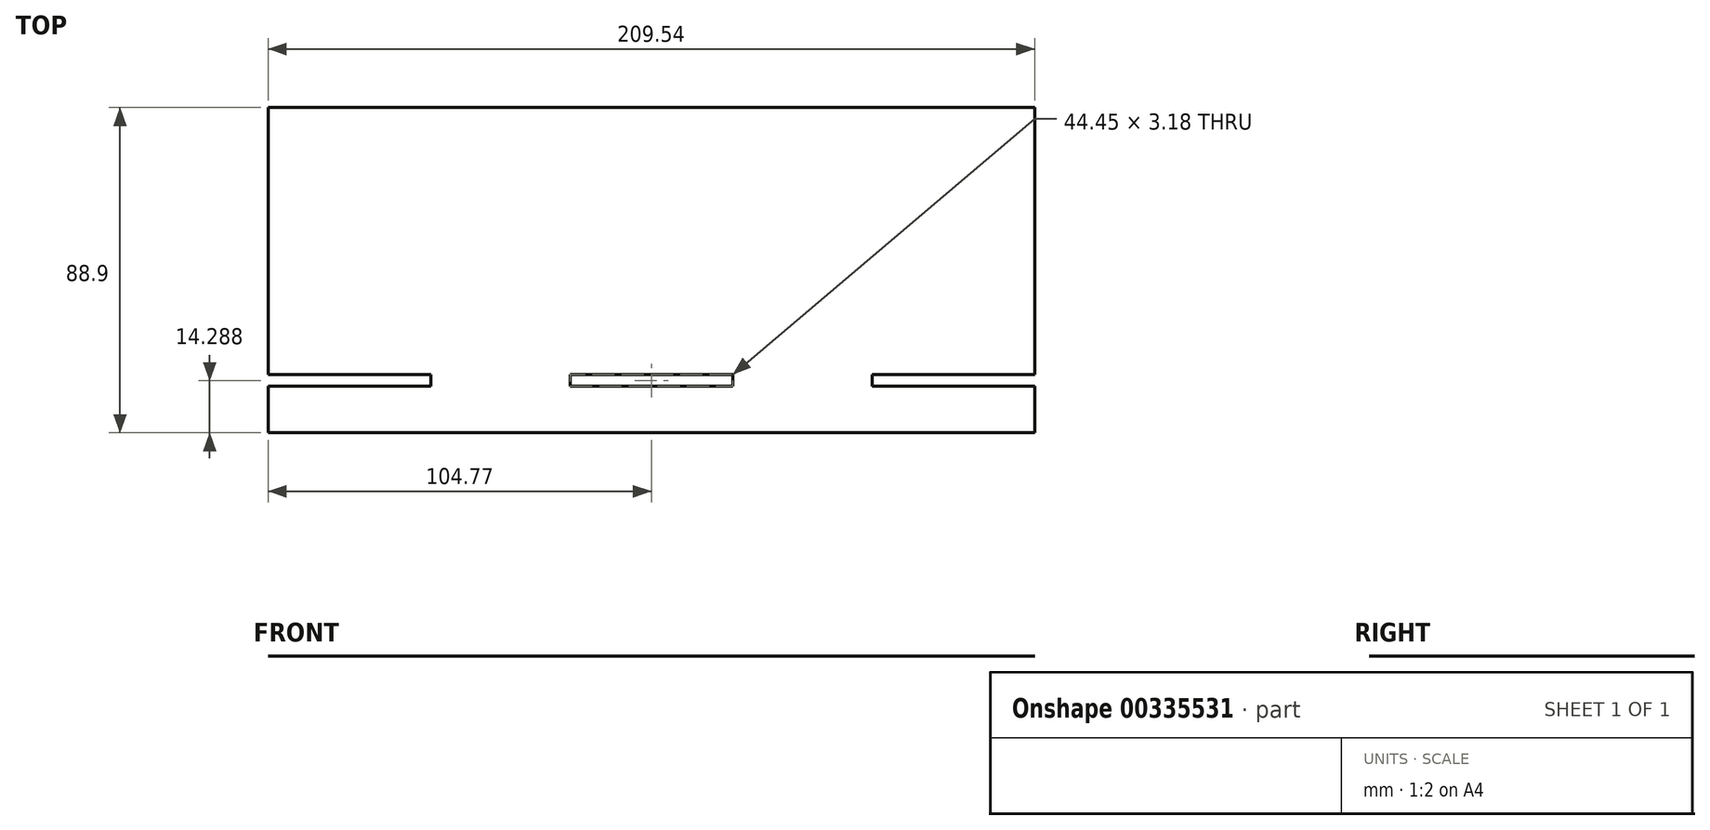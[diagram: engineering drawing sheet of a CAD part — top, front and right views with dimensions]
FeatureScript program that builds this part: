
annotation { "Feature Type Name" : "Feature", "Feature Type Description" : "" }
export const myFeature = defineFeature(function(context is Context, id is Id, definition is map)
    precondition{}
    {
        {
            var Q0;
            Q0=qCreatedBy(makeId("Top.planeOp"),FACE);
            var sketch = newSketch(context, id + "F0", { "sketchPlane" : qUnion([Q0])});
            skLineSegment(sketch, "E0.bottom", {"start": v(104.78, -44.45) * mm, "end": v(-104.77, -44.45) * mm});
            skLineSegment(sketch, "E0.top", {"start": v(104.77, 44.45) * mm, "end": v(-104.78, 44.45) * mm});
            skLineSegment(sketch, "E0.left", {"start": v(104.78, -44.45) * mm, "end": v(104.77, 44.45) * mm});
            skLineSegment(sketch, "E0.right", {"start": v(-104.77, -44.45) * mm, "end": v(-104.78, 44.45) * mm});
            skPoint(sketch, "E0.middle", {"position": v(0, 0) * mm});
            skSolve(sketch);
        }
        {
            var Q0;
            Q0=makeQuery(id+"F0.imprint","IMPRINT",FACE,{"disambiguationData":[TD([[makeQuery(id+"F0.imprint","IMPRINT",EDGE,{"derivedFrom":sQuery(id+"F0.wireOp",EDGE,"E0.bottom")}),-1.0]])]});
            extrude(context, id + "F1", {"entities" : qUnion([Q0]), "depth" : 1 / 203.2 * mm});
        }
        {
            var Q0;
            Q0=makeQuery(id+"F1.opExtrude","CAP_FACE",FACE,{"disambiguationData":[OSD([sQuery(id+"F0.wireOp",EDGE,"E0.bottom"),sQuery(id+"F0.wireOp",EDGE,"E0.top"),sQuery(id+"F0.wireOp",EDGE,"E0.left"),sQuery(id+"F0.wireOp",EDGE,"E0.right")])],"isStart":false});
            var sketch = newSketch(context, id + "F2", { "sketchPlane" : qUnion([Q0])});
            skLineSegment(sketch, "E1.bottom", {"start": v(-104.77, -28.58) * mm, "end": v(-60.32, -28.58) * mm});
            skLineSegment(sketch, "E1.top", {"start": v(-104.77, -31.75) * mm, "end": v(-60.32, -31.75) * mm});
            skLineSegment(sketch, "E1.left", {"start": v(-104.77, -28.57) * mm, "end": v(-104.77, -31.75) * mm});
            skLineSegment(sketch, "E1.right", {"start": v(-60.32, -28.57) * mm, "end": v(-60.32, -31.75) * mm});
            skLineSegment(sketch, "E2.right", {"start": v(104.77, -28.57) * mm, "end": v(104.77, -31.75) * mm});
            skLineSegment(sketch, "E3.bottom", {"start": v(60.33, -28.57) * mm, "end": v(104.78, -28.57) * mm});
            skLineSegment(sketch, "E3.top", {"start": v(60.33, -31.75) * mm, "end": v(104.78, -31.75) * mm});
            skLineSegment(sketch, "E3.left", {"start": v(60.33, -28.57) * mm, "end": v(60.33, -31.75) * mm});
            skLineSegment(sketch, "E3.right", {"start": v(104.78, -28.57) * mm, "end": v(104.78, -31.75) * mm});
            skLineSegment(sketch, "E4.bottom", {"start": v(22.23, -31.75) * mm, "end": v(-22.23, -31.75) * mm});
            skLineSegment(sketch, "E4.top", {"start": v(22.23, -28.58) * mm, "end": v(-22.23, -28.58) * mm});
            skLineSegment(sketch, "E4.left", {"start": v(22.23, -31.75) * mm, "end": v(22.23, -28.58) * mm});
            skLineSegment(sketch, "E4.right", {"start": v(-22.23, -31.75) * mm, "end": v(-22.23, -28.58) * mm});
            skPoint(sketch, "E4.middle", {"position": v(0, -30.16) * mm});
            skSolve(sketch);
        }
        {
            var Q0;
            Q0 = qSketchRegion(id + "F2", true);
            extrude(context, id + "F3", {"entities" : qUnion([Q0]), "operationType" : NewBodyOperationType.REMOVE, "oppositeDirection" : true, "depth" : 25.4 * mm});
        }
    });
